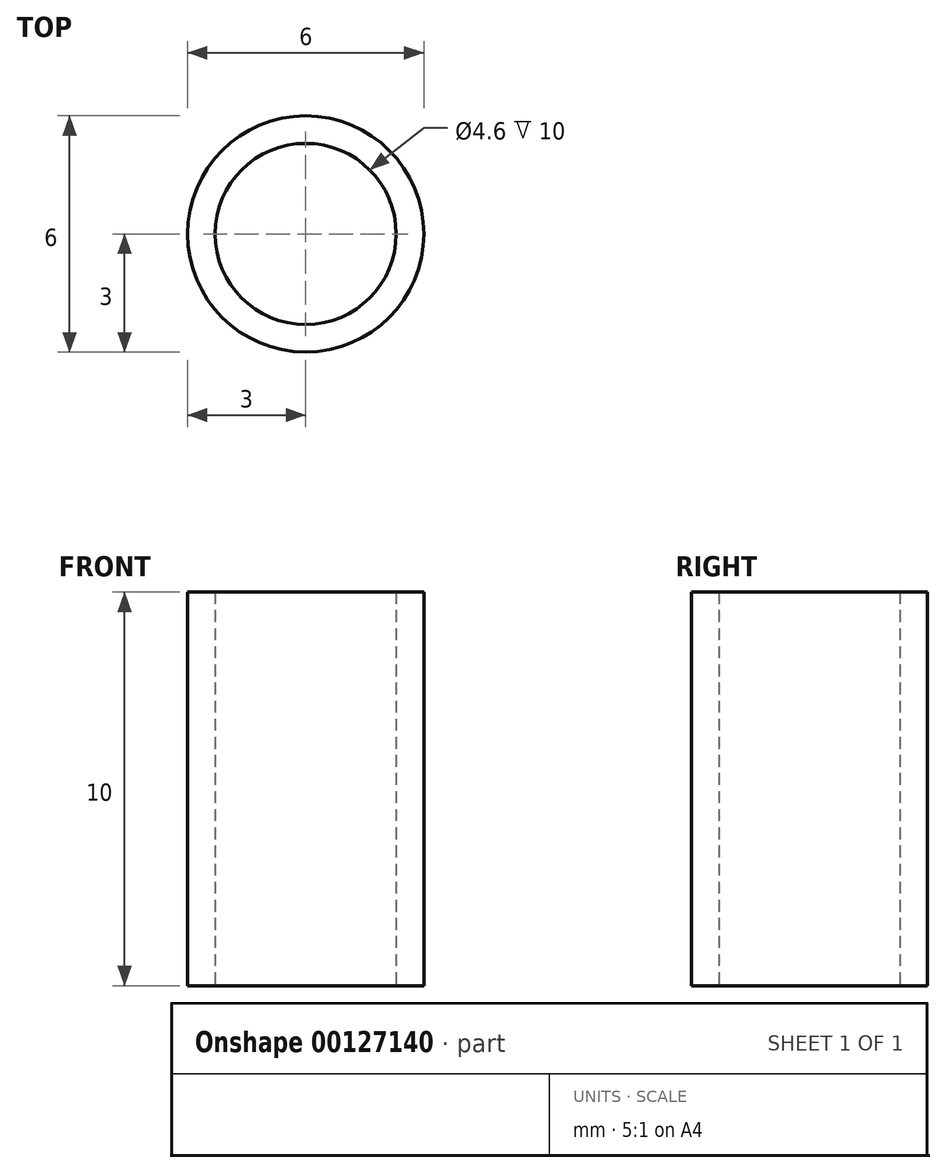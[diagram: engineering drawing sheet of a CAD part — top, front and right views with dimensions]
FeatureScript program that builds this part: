
annotation { "Feature Type Name" : "Feature", "Feature Type Description" : "" }
export const myFeature = defineFeature(function(context is Context, id is Id, definition is map)
    precondition{}
    {
        {
            var Q0;
            Q0=qCreatedBy(makeId("Top.planeOp"),FACE);
            var sketch = newSketch(context, id + "F0", { "sketchPlane" : qUnion([Q0])});
            skCircle(sketch, "E0", {"center": v(0, 0) * mm, "radius": 3 * mm});
            skCircle(sketch, "E1", {"center": v(0, 0) * mm, "radius": 2.3 * mm});
            skSolve(sketch);
        }
        {
            var Q0;
            Q0=makeQuery(id+"F0.imprint","IMPRINT",FACE,{"disambiguationData":[TD([[makeQuery(id+"F0.imprint","IMPRINT",EDGE,{"derivedFrom":sQuery(id+"F0.wireOp",EDGE,"E0")}),1.0]])]});
            extrude(context, id + "F1", {"entities" : qUnion([Q0]), "depth" : 10 * mm});
        }
    });
